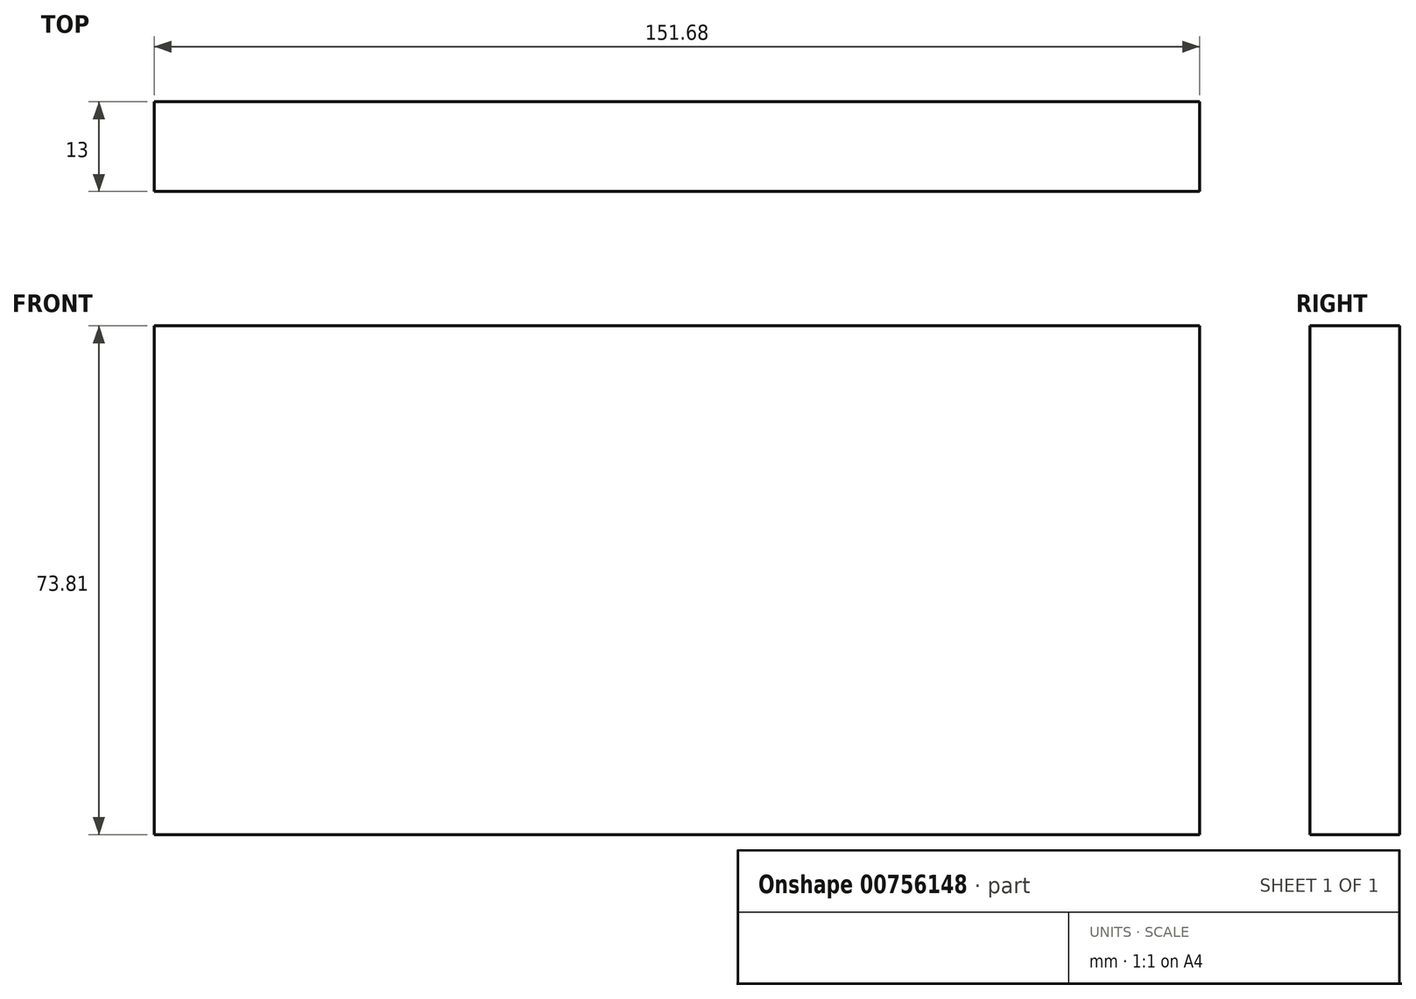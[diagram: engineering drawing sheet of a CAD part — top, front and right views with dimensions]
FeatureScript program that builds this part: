
annotation { "Feature Type Name" : "Feature", "Feature Type Description" : "" }
export const myFeature = defineFeature(function(context is Context, id is Id, definition is map)
    precondition{}
    {
        {
            var Q0;
            Q0=qCreatedBy(makeId("Front.planeOp"),FACE);
            var sketch = newSketch(context, id + "F0", { "sketchPlane" : qUnion([Q0])});
            skLineSegment(sketch, "E0.bottom", {"start": v(-76.02, -32.22) * mm, "end": v(75.66, -32.22) * mm});
            skLineSegment(sketch, "E0.top", {"start": v(-76.02, 41.59) * mm, "end": v(75.66, 41.59) * mm});
            skLineSegment(sketch, "E0.left", {"start": v(-76.02, -32.22) * mm, "end": v(-76.02, 41.59) * mm});
            skLineSegment(sketch, "E0.right", {"start": v(75.66, -32.22) * mm, "end": v(75.66, 41.59) * mm});
            skSolve(sketch);
        }
        {
            var Q0;
            Q0=makeQuery(id+"F0.imprint","IMPRINT",FACE,{"disambiguationData":[TD([[makeQuery(id+"F0.imprint","IMPRINT",EDGE,{"derivedFrom":sQuery(id+"F0.wireOp",EDGE,"E0.bottom")}),1.0]])]});
            extrude(context, id + "F1", {"entities" : qUnion([Q0]), "depth" : 13 * mm, "offsetDistance" : 25 * mm});
        }
    });
